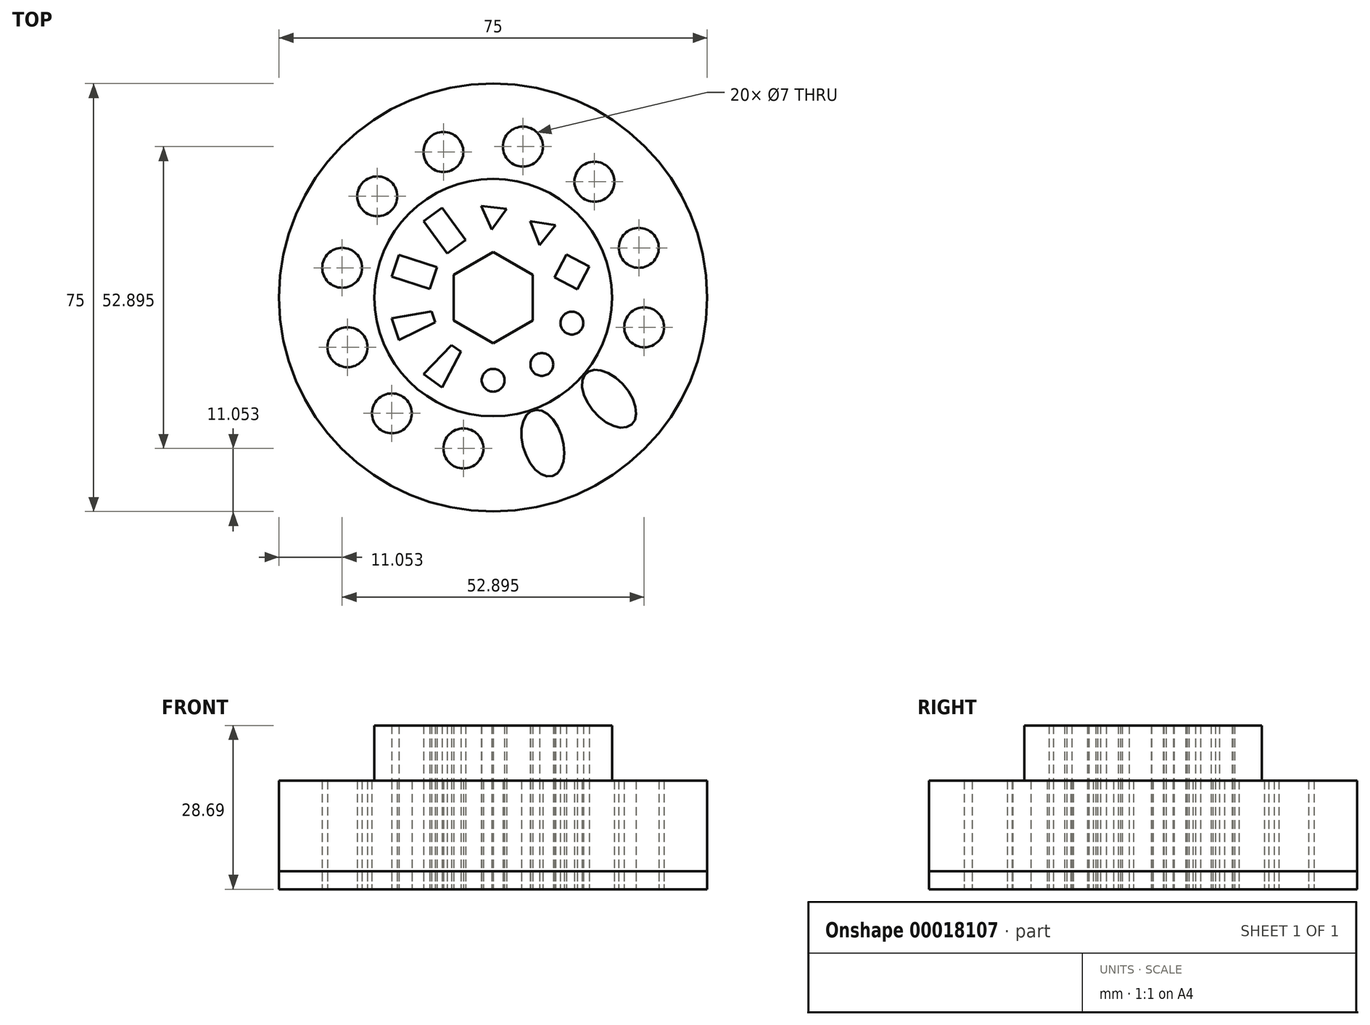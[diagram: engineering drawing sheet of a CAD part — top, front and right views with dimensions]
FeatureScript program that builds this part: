
annotation { "Feature Type Name" : "Feature", "Feature Type Description" : "" }
export const myFeature = defineFeature(function(context is Context, id is Id, definition is map)
    precondition{}
    {
        {
            var Q0;
            Q0=qCreatedBy(makeId("Top.planeOp"),FACE);
            var sketch = newSketch(context, id + "F0", { "sketchPlane" : qUnion([Q0])});
            skCircle(sketch, "E0", {"center": v(0, 0) * mm, "radius": 37.5 * mm});
            skCircle(sketch, "E1.0", {"center": v(0, 0) * mm, "radius": 44.88 * mm});
            skSolve(sketch);
        }
        {
            var Q0;
            Q0=makeQuery(id+"F0.imprint","IMPRINT",FACE,{"disambiguationData":[TD([[makeQuery(id+"F0.imprint","IMPRINT",EDGE,{"derivedFrom":sQuery(id+"F0.wireOp",EDGE,"E0")}),1.0]])]});
            extrude(context, id + "F1", {"entities" : qUnion([Q0]), "depth" : 19 * mm});
        }
        {
            var Q0;
            Q0=makeQuery(id+"F0.imprint","IMPRINT",FACE,{"disambiguationData":[TD([[makeQuery(id+"F0.imprint","IMPRINT",EDGE,{"derivedFrom":sQuery(id+"F0.wireOp",EDGE,"E0")}),-1.0]])]});
            var Q1;
            Q1=makeQuery(id+"F0.imprint","IMPRINT",FACE,{"disambiguationData":[TD([[makeQuery(id+"F0.imprint","IMPRINT",EDGE,{"derivedFrom":sQuery(id+"F0.wireOp",EDGE,"E0")}),1.0]])]});
            extrude(context, id + "F2", {"entities" : qUnion([Q0, Q1]), "depth" : 3.17 * mm});
        }
        {
            var Q0;
            Q0=qCreatedBy(makeId("Top.planeOp"),FACE);
            var sketch = newSketch(context, id + "F3", { "sketchPlane" : qUnion([Q0])});
            skCircle(sketch, "E2.cCircle", {"center": v(0, 0) * mm, "radius": 8 * mm, "construction": true});
            skLineSegment(sketch, "E2.0", {"start": v(6.93, 4) * mm, "end": v(6.93, -4) * mm});
            skLineSegment(sketch, "E2.1", {"start": v(6.93, -4) * mm, "end": v(0, -8) * mm});
            skLineSegment(sketch, "E2.2", {"start": v(0, -8) * mm, "end": v(-6.93, -4) * mm});
            skLineSegment(sketch, "E2.3", {"start": v(-6.93, -4) * mm, "end": v(-6.93, 4) * mm});
            skLineSegment(sketch, "E2.4", {"start": v(-6.93, 4) * mm, "end": v(0, 8) * mm});
            skLineSegment(sketch, "E2.5", {"start": v(0, 8) * mm, "end": v(6.93, 4) * mm});
            skCircle(sketch, "E3.cCircle", {"center": v(0, 0) * mm, "radius": 14.5 * mm, "construction": true});
            skLineSegment(sketch, "E3.0", {"start": v(0, 14.5) * mm, "end": v(8.52, 11.73) * mm});
            skLineSegment(sketch, "E3.1", {"start": v(8.52, 11.73) * mm, "end": v(13.8, 4.48) * mm});
            skLineSegment(sketch, "E3.2", {"start": v(13.8, 4.48) * mm, "end": v(13.8, -4.48) * mm});
            skLineSegment(sketch, "E3.3", {"start": v(13.8, -4.48) * mm, "end": v(8.52, -11.73) * mm});
            skLineSegment(sketch, "E3.4", {"start": v(8.52, -11.73) * mm, "end": v(0, -14.5) * mm});
            skLineSegment(sketch, "E3.5", {"start": v(0, -14.5) * mm, "end": v(-8.52, -11.73) * mm});
            skLineSegment(sketch, "E3.6", {"start": v(-8.52, -11.73) * mm, "end": v(-13.8, -4.48) * mm});
            skLineSegment(sketch, "E3.7", {"start": v(-13.8, -4.48) * mm, "end": v(-13.8, 4.48) * mm});
            skLineSegment(sketch, "E3.8", {"start": v(-13.8, 4.48) * mm, "end": v(-8.52, 11.73) * mm});
            skLineSegment(sketch, "E3.9", {"start": v(-8.52, 11.73) * mm, "end": v(0, 14.5) * mm});
            skCircle(sketch, "E4.cCircle", {"center": v(0, 14.5) * mm, "radius": 2.6 * mm, "construction": true});
            skLineSegment(sketch, "E4.0", {"start": v(2.37, 15.57) * mm, "end": v(-0.26, 11.91) * mm});
            skLineSegment(sketch, "E4.1", {"start": v(-0.26, 11.91) * mm, "end": v(-2.1, 16.02) * mm});
            skLineSegment(sketch, "E4.2", {"start": v(-2.1, 16.02) * mm, "end": v(2.37, 15.57) * mm});
            skCircle(sketch, "E5.cCircle", {"center": v(8.52, 11.73) * mm, "radius": 2.6 * mm, "construction": true});
            skLineSegment(sketch, "E5.0", {"start": v(10.95, 12.66) * mm, "end": v(8.11, 9.17) * mm});
            skLineSegment(sketch, "E5.1", {"start": v(8.11, 9.17) * mm, "end": v(6.5, 13.37) * mm});
            skLineSegment(sketch, "E5.2", {"start": v(6.5, 13.37) * mm, "end": v(10.95, 12.66) * mm});
            skCircle(sketch, "E6.cCircle", {"center": v(13.8, 4.48) * mm, "radius": 3.18 * mm, "construction": true});
            skLineSegment(sketch, "E6.0", {"start": v(16.82, 5.44) * mm, "end": v(14.75, 1.45) * mm});
            skLineSegment(sketch, "E6.1", {"start": v(14.75, 1.45) * mm, "end": v(10.76, 3.52) * mm});
            skLineSegment(sketch, "E6.2", {"start": v(10.76, 3.52) * mm, "end": v(12.83, 7.51) * mm});
            skLineSegment(sketch, "E6.3", {"start": v(12.83, 7.51) * mm, "end": v(16.82, 5.44) * mm});
            skCircle(sketch, "E7", {"center": v(0, -14.5) * mm, "radius": 2 * mm});
            skCircle(sketch, "E8", {"center": v(13.8, -4.48) * mm, "radius": 2 * mm});
            skLineSegment(sketch, "E9", {"start": v(-10.46, 3.4) * mm, "end": v(-17.12, 5.56) * mm, "construction": true});
            skLineSegment(sketch, "E10", {"start": v(-10.46, -3.4) * mm, "end": v(-17.12, -5.56) * mm, "construction": true});
            skLineSegment(sketch, "E11", {"start": v(-6.47, 8.9) * mm, "end": v(-10.58, 14.56) * mm, "construction": true});
            skLineSegment(sketch, "E12", {"start": v(-10.58, 14.56) * mm, "end": v(-8.52, 11.73) * mm, "construction": true});
            skPoint(sketch, "E13", {"position": v(-8.52, 11.73) * mm});
            skPoint(sketch, "E14", {"position": v(-13.8, 4.48) * mm});
            skLineSegment(sketch, "E15", {"start": v(-6.47, -8.9) * mm, "end": v(-10.58, -14.56) * mm, "construction": true});
            skPoint(sketch, "E16", {"position": v(-13.8, -4.48) * mm});
            skPoint(sketch, "E17", {"position": v(-8.52, -11.73) * mm});
            skLineSegment(sketch, "E18", {"start": v(-8.97, 15.74) * mm, "end": v(-12.2, 13.38) * mm, "construction": true});
            skPoint(sketch, "E19", {"position": v(-10.58, 14.56) * mm});
            skLineSegment(sketch, "E20", {"start": v(-4.85, 10.07) * mm, "end": v(-8.08, 7.72) * mm, "construction": true});
            skPoint(sketch, "E21", {"position": v(-6.47, 8.9) * mm});
            skLineSegment(sketch, "E22", {"start": v(-12.2, 13.38) * mm, "end": v(-8.08, 7.72) * mm});
            skLineSegment(sketch, "E23", {"start": v(-8.08, 7.72) * mm, "end": v(-4.85, 10.07) * mm});
            skLineSegment(sketch, "E24", {"start": v(-4.85, 10.07) * mm, "end": v(-8.97, 15.74) * mm});
            skLineSegment(sketch, "E25", {"start": v(-8.97, 15.74) * mm, "end": v(-12.2, 13.38) * mm});
            skLineSegment(sketch, "E26", {"start": v(-17.74, 3.66) * mm, "end": v(-16.5, 7.46) * mm, "construction": true});
            skLineSegment(sketch, "E27", {"start": v(-11.08, 1.5) * mm, "end": v(-9.84, 5.3) * mm, "construction": true});
            skPoint(sketch, "E28", {"position": v(-17.12, 5.56) * mm});
            skPoint(sketch, "E29", {"position": v(-10.46, 3.4) * mm});
            skLineSegment(sketch, "E30", {"start": v(-17.74, 3.66) * mm, "end": v(-16.5, 7.46) * mm});
            skLineSegment(sketch, "E31", {"start": v(-16.5, 7.46) * mm, "end": v(-9.84, 5.3) * mm});
            skLineSegment(sketch, "E32", {"start": v(-9.84, 5.3) * mm, "end": v(-11.08, 1.5) * mm});
            skLineSegment(sketch, "E33", {"start": v(-11.08, 1.5) * mm, "end": v(-17.74, 3.66) * mm});
            skLineSegment(sketch, "E34", {"start": v(-17.74, -3.66) * mm, "end": v(-16.5, -7.46) * mm, "construction": true});
            skLineSegment(sketch, "E35", {"start": v(-12.2, -13.39) * mm, "end": v(-8.96, -15.74) * mm, "construction": true});
            skPoint(sketch, "E36", {"position": v(-17.12, -5.56) * mm});
            skPoint(sketch, "E37", {"position": v(-10.58, -14.56) * mm});
            skLineSegment(sketch, "E38", {"start": v(-10.77, -2.45) * mm, "end": v(-10.15, -4.35) * mm, "construction": true});
            skLineSegment(sketch, "E39", {"start": v(-7.27, -8.31) * mm, "end": v(-5.66, -9.49) * mm, "construction": true});
            skPoint(sketch, "E40", {"position": v(-10.46, -3.4) * mm});
            skPoint(sketch, "E41", {"position": v(-6.47, -8.9) * mm});
            skLineSegment(sketch, "E42", {"start": v(-17.74, -3.66) * mm, "end": v(-10.77, -2.45) * mm});
            skLineSegment(sketch, "E43", {"start": v(-10.77, -2.45) * mm, "end": v(-10.15, -4.35) * mm});
            skLineSegment(sketch, "E44", {"start": v(-10.15, -4.35) * mm, "end": v(-16.5, -7.46) * mm});
            skLineSegment(sketch, "E45", {"start": v(-16.5, -7.46) * mm, "end": v(-17.74, -3.66) * mm});
            skLineSegment(sketch, "E46", {"start": v(-12.2, -13.39) * mm, "end": v(-8.96, -15.74) * mm});
            skLineSegment(sketch, "E47", {"start": v(-8.96, -15.74) * mm, "end": v(-5.66, -9.49) * mm});
            skLineSegment(sketch, "E48", {"start": v(-5.66, -9.49) * mm, "end": v(-7.27, -8.31) * mm});
            skLineSegment(sketch, "E49", {"start": v(-7.27, -8.31) * mm, "end": v(-12.2, -13.39) * mm});
            skCircle(sketch, "E50.0", {"center": v(0, 0) * mm, "radius": 37.5 * mm});
            skCircle(sketch, "E51", {"center": v(8.52, -11.73) * mm, "radius": 2 * mm});
            skCircle(sketch, "E52.cCircle", {"center": v(0, 0) * mm, "radius": 26.96 * mm, "construction": true});
            skLineSegment(sketch, "E52.0", {"start": v(-26.45, 5.21) * mm, "end": v(-20.3, 17.74) * mm});
            skLineSegment(sketch, "E52.1", {"start": v(-20.3, 17.74) * mm, "end": v(-8.7, 25.51) * mm});
            skLineSegment(sketch, "E52.2", {"start": v(-8.7, 25.51) * mm, "end": v(5.21, 26.45) * mm});
            skLineSegment(sketch, "E52.3", {"start": v(5.21, 26.45) * mm, "end": v(17.74, 20.3) * mm});
            skLineSegment(sketch, "E52.4", {"start": v(17.74, 20.3) * mm, "end": v(25.51, 8.7) * mm});
            skLineSegment(sketch, "E52.5", {"start": v(25.51, 8.7) * mm, "end": v(26.45, -5.21) * mm});
            skLineSegment(sketch, "E52.6", {"start": v(26.45, -5.21) * mm, "end": v(20.3, -17.74) * mm});
            skLineSegment(sketch, "E52.7", {"start": v(20.3, -17.74) * mm, "end": v(8.7, -25.51) * mm});
            skLineSegment(sketch, "E52.8", {"start": v(8.7, -25.51) * mm, "end": v(-5.21, -26.45) * mm});
            skLineSegment(sketch, "E52.9", {"start": v(-5.21, -26.45) * mm, "end": v(-17.74, -20.3) * mm});
            skLineSegment(sketch, "E52.10", {"start": v(-17.74, -20.3) * mm, "end": v(-25.51, -8.7) * mm});
            skLineSegment(sketch, "E52.11", {"start": v(-25.51, -8.7) * mm, "end": v(-26.45, 5.21) * mm});
            skCircle(sketch, "E53", {"center": v(-20.3, 17.74) * mm, "radius": 3.5 * mm});
            skCircle(sketch, "E54.1.0", {"center": v(-8.7, 25.51) * mm, "radius": 3.5 * mm});
            skCircle(sketch, "E54.2.0", {"center": v(5.21, 26.45) * mm, "radius": 3.5 * mm});
            skCircle(sketch, "E54.3.0", {"center": v(17.74, 20.3) * mm, "radius": 3.5 * mm});
            skCircle(sketch, "E54.4.0", {"center": v(25.51, 8.7) * mm, "radius": 3.5 * mm});
            skCircle(sketch, "E54.5.0", {"center": v(26.45, -5.21) * mm, "radius": 3.5 * mm});
            skCircle(sketch, "E54.8.0", {"center": v(-5.21, -26.45) * mm, "radius": 3.5 * mm});
            skCircle(sketch, "E54.9.0", {"center": v(-17.74, -20.3) * mm, "radius": 3.5 * mm});
            skCircle(sketch, "E54.10.0", {"center": v(-25.51, -8.7) * mm, "radius": 3.5 * mm});
            skCircle(sketch, "E54.11.0", {"center": v(-26.45, 5.21) * mm, "radius": 3.5 * mm});
            skLineSegment(sketch, "E54.anchor1", {"start": v(0, 0) * mm, "end": v(-20.3, 17.74) * mm, "construction": true});
            skLineSegment(sketch, "E54.anchor2", {"start": v(0, 0) * mm, "end": v(-26.45, 5.21) * mm, "construction": true});
            skEllipse(sketch, "E55", {"center": v(8.7, -25.51) * mm, "majorRadius": 6 * mm, "minorRadius": 3.5 * mm, "majorAxis": v(0.28, -0.96)});
            skEllipse(sketch, "E56", {"center": v(20.3, -17.74) * mm, "majorRadius": 6 * mm, "minorRadius": 3.5 * mm, "majorAxis": v(0.66, -0.75)});
            skSolve(sketch);
        }
        {
            var Q0;
            Q0=makeQuery(id+"F1.opExtrude","CAP_FACE",FACE,{"disambiguationData":[OSD([sQuery(id+"F0.wireOp",EDGE,"E0")])],"isStart":false});
            var sketch = newSketch(context, id + "F4", { "sketchPlane" : qUnion([Q0])});
            skCircle(sketch, "E57", {"center": v(0, 0) * mm, "radius": 20.8 * mm});
            skSolve(sketch);
        }
        {
            var Q0;
            Q0 = qSketchRegion(id + "F4", true);
            extrude(context, id + "F5", {"entities" : qUnion([Q0]), "depth" : 9.7 * mm});
        }
        {
            var Q0;
            Q0=makeQuery(id+"F3.imprint","IMPRINT",FACE,{"disambiguationData":[TD([[makeQuery(id+"F3.imprint","IMPRINT",EDGE,{"derivedFrom":sQuery(id+"F3.wireOp",EDGE,"E50.0")}),1.0]])]});
            var Q1;
            {var subQ47=sQuery(id+"F3.wireOp",EDGE,"E4.2");Q1=makeQuery(id+"F3.imprint","IMPRINT",FACE,{"disambiguationData":[TD([[makeQuery(id+"F3.imprint","IMPRINT",EDGE,{"derivedFrom":subQ47}),1.0]])]});}
            var Q2;
            Q2=makeQuery(id+"F3.imprint","IMPRINT",FACE,{"disambiguationData":[TD([[makeQuery(id+"F3.imprint","IMPRINT",EDGE,{"derivedFrom":sQuery(id+"F3.wireOp",EDGE,"E2.0")}),1.0]])]});
            extrude(context, id + "F6", {"entities" : qUnion([Q0, Q1, Q2]), "operationType" : NewBodyOperationType.INTERSECT, "endBound" : BoundingType.THROUGH_ALL, "depth" : 25 * mm});
        }
    });
